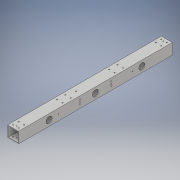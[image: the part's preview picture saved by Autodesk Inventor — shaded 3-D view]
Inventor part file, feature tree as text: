
AUTODESK INVENTOR PART (.ipt)
format: ipt  version: 2018 (Build 220112000, 112)  size: 306,688 bytes
history: native  units: in
note: dims shown in document units (in); Inventor stores cm internally (conversion verified against a paired STEP export)
features: extrude x3, sketch x3
ambient origin geometry x8: Origin, YZ Plane, XZ Plane, XY Plane, X Axis, Y Axis, Z Axis, Center Point
bodies: Solid2 (feature_tree), Solid1 (feature_tree)
feature tree (6):
  extrude  "Extrusion1"  Depth=8.5in
  extrude  "Extrusion3"  Depth=0.2in
  extrude  "Extrusion4"  Depth=0.125in TaperAngle=0.0deg
  sketch  "Sketch1"  dims[d0=0.5in d1=8.5in]
  sketch  "Sketch2"  dims[d2=1.5in d3=0.2in]
  sketch  "Sketch3"  dims[d4=13.4375in d5=0.0in d8=0.125in d9=0.0in d10=0.125in d11=0.0in]
